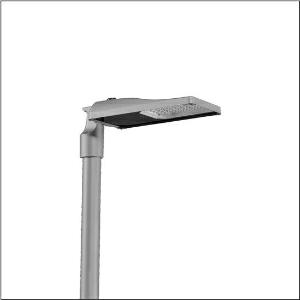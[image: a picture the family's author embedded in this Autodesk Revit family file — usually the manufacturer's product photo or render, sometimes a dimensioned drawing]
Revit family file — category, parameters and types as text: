
# Revit family: streetlight_sl_31_mini___st1_0a_5xh2d3as08ja_29fe
name_source: partatom
category: Lighting Fixtures
units: mm (PartAtom-declared; Revit-internal decimal feet)

## family parameters
Cut with Voids When Loaded = No
Host = Face
Light Source = No
Part Type = Normal
Room Calculation Point = No
Round Connector Dimension = Use Diameter
Shared = No

## types (1)
- --- (1 x LED, 12270 lm, 82.5 W, 3000K)
    Apparent Load = 83 VA
    CIE Flux Codes = 40 73 97 100 100
    Color Rendering = 70
    Color Temperature = 3000K
    Default Elevation = 1800 mm
    Description = Streetlight SL 31 mini, mast luminaire, primary light control with lens, of PMMA, primary optical cover: cover, of toughened safety glass, transparent, light distribution: ST1.0a, light emission: direct distribution, primary light characteristic: asymmetric, installation type: post-top, side-entry, LED, High Power LED, rated luminous flux: 12.270lm, luminous efficacy: 149lm/W, light colour: 730, colour temperature: 3000K, control: presetting dimming logarithmic, flexible luminous flux parameterisation, time-dependent luminous flux control, constant luminous flux control, power reduction, intelligent temperature release in ECG and LED module, overheat protection, with cable H07RN-F 2x 1.5mm², mains connection: 220..240V, AC, 50/60Hz, connection cable pre-assembled, cable length: 10,5m, start of lifetime: 83W, end of service life: 90W, reduction: 37W, luminaire housing, of diecast aluminium, powder-coated, Siteco® metallic grey (DB 702S), corrosivity category C5 high according to DIN EN ISO 12944, no sealing on luminaire upper side, inclination: -15°..+20° (post-top) | -20°..+20° (side-entry), adjustable in 5° steps, mast flange (76/60mm) included as standard, multi-level sealing system, sealing non-destructively replaceable, Smart Interface above, protection rating (complete): IP66, insulation class (complete): insulation class II (safety insulation), certification: CE, ENEC, ENEC+, VDE, UKCA, ZD4i, impact resistance: IK09, permissible operating ambient temperature for outdoor applications: -40..+50°C, standard-compliant lighting for roads and squares, packaging unit: 1 piece

Light Distribution: ST1.0a
    Height = 76 mm
    Lamp = 1 x LED
    Lamp Light Flux = 12270 lm
    Lamp Power = 82.5 W
    Lamp count = 1
    Length = 547 mm
    Luminous efficacy = 149 lm/W
    Manufacturer = Siteco
    ModVariant = No
    Model = 5XH2D3AS08JA
    Number of Poles = 1
    OnlyDefault = Yes
    Power Factor = 1
    Product Name = Streetlight SL 31 mini | ST1.0a
    Product group = mast luminaire | pylon top
    ProductGroupID = 6100
    Protection Class = Protection class II
    Protection Degree = IP 66
    RLX_Detail_Level = 1
    RLX_Emergency_Light_Flux = 0 lm
    RLX_Emergency_Type = 0
    RLX_Emergency_Type_DB = No
    RlxData = <blob elided: 39961 chars, md5=ba9e7d15>
    Socket = socket
    Standby Power = 0 W
    System Light Flux = 12270 lm
    System Power = 83 W
    Type Comments = factory setting: luminous flux: 100 % | dim-lin: 254 | 870 mA
    Type Image = l_1300330.jpg
    URL = http://relux.com
    VarID = @adj_008455
    Voltage = 0 V
    Weight = 0.00 kg
    Width = 265 mm

## geometry (parser evidence)
native form markers: Blend x4, Sweep x9
no freeform markers — native parametric forms only
